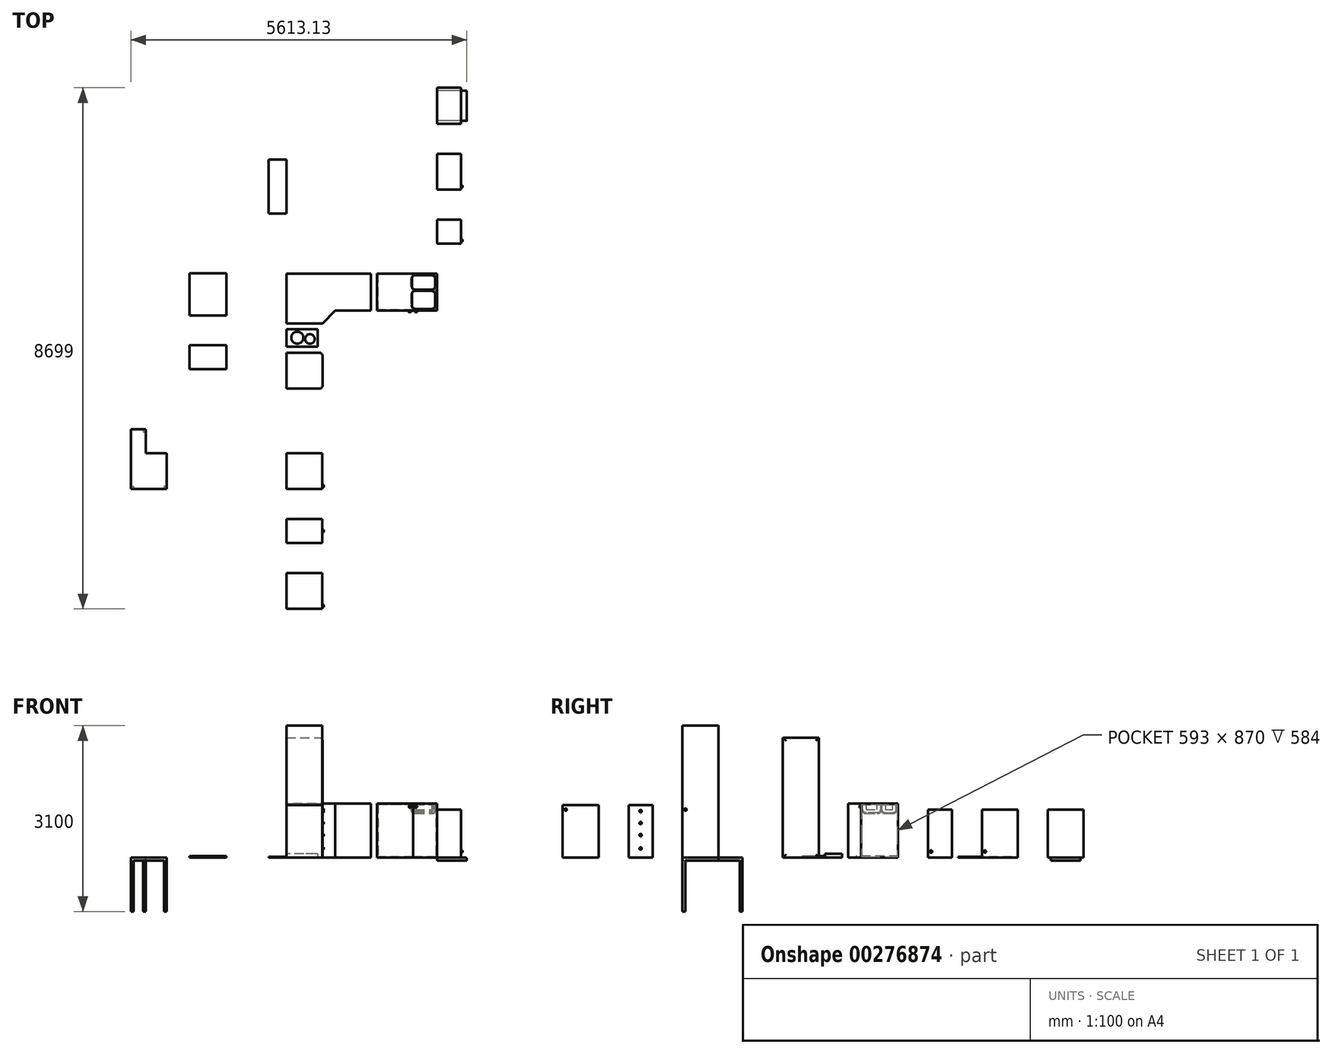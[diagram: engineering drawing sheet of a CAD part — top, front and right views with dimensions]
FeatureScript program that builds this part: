
annotation { "Feature Type Name" : "Feature", "Feature Type Description" : "" }
export const myFeature = defineFeature(function(context is Context, id is Id, definition is map)
    precondition{}
    {
        {
            var Q0;
            Q0=qCreatedBy(makeId("Top.planeOp"),FACE);
            var sketch = newSketch(context, id + "F0", { "sketchPlane" : qUnion([Q0])});
            skLineSegment(sketch, "E0.bottom", {"start": v(0, 0) * mm, "end": v(2000, 0) * mm});
            skLineSegment(sketch, "E0.left", {"start": v(0, 0) * mm, "end": v(0, -2000) * mm});
            skLineSegment(sketch, "E1", {"start": v(2000, 0) * mm, "end": v(2000, 120) * mm});
            skLineSegment(sketch, "E2", {"start": v(2000, 120) * mm, "end": v(-120, 120) * mm});
            skLineSegment(sketch, "E3", {"start": v(-120, 120) * mm, "end": v(-120, -2000) * mm});
            skLineSegment(sketch, "E4", {"start": v(-120, -2000) * mm, "end": v(0, -2000) * mm});
            skLineSegment(sketch, "E5", {"start": v(1300, 120) * mm, "end": v(1300, 0) * mm});
            skPoint(sketch, "E5.endSnap0", {"position": v(1000, 0) * mm});
            skLineSegment(sketch, "E6", {"start": v(1900, 120) * mm, "end": v(1900, 0) * mm});
            skSolve(sketch);
        }
        {
            var Q0;
            Q0=qCreatedBy(makeId("Top.planeOp"),FACE);
            var sketch = newSketch(context, id + "F1", { "sketchPlane" : qUnion([Q0])});
            skLineSegment(sketch, "E7.bottom", {"start": v(1, -1323.13) * mm, "end": v(601, -1323.13) * mm});
            skLineSegment(sketch, "E7.top", {"start": v(1, -1923.13) * mm, "end": v(601, -1923.13) * mm});
            skLineSegment(sketch, "E7.left", {"start": v(1, -1323.13) * mm, "end": v(1, -1923.13) * mm});
            skLineSegment(sketch, "E7.right", {"start": v(601, -1323.13) * mm, "end": v(601, -1923.13) * mm});
            skLineSegment(sketch, "E8.bottom", {"start": v(521, -1223.13) * mm, "end": v(1, -1223.13) * mm});
            skLineSegment(sketch, "E8.top", {"start": v(521, -933.13) * mm, "end": v(1, -933.13) * mm});
            skLineSegment(sketch, "E8.left", {"start": v(521, -1223.13) * mm, "end": v(521, -933.13) * mm});
            skLineSegment(sketch, "E8.right", {"start": v(1, -1223.13) * mm, "end": v(1, -933.13) * mm});
            skLineSegment(sketch, "E9", {"start": v(601, -833.13) * mm, "end": v(813.13, -621) * mm});
            skLineSegment(sketch, "E10", {"start": v(813.13, -621) * mm, "end": v(1413.13, -621) * mm});
            skLineSegment(sketch, "E11", {"start": v(1413.13, -621) * mm, "end": v(1413.13, -1) * mm});
            skLineSegment(sketch, "E12", {"start": v(1413.13, -1) * mm, "end": v(1, -1) * mm});
            skLineSegment(sketch, "E13", {"start": v(1, -1) * mm, "end": v(1, -833.13) * mm});
            skLineSegment(sketch, "E14", {"start": v(1, -833.13) * mm, "end": v(601, -833.13) * mm});
            skLineSegment(sketch, "E15.bottom", {"start": v(2513.13, -621) * mm, "end": v(1513.13, -621) * mm});
            skLineSegment(sketch, "E15.top", {"start": v(2513.13, -1) * mm, "end": v(1513.13, -1) * mm});
            skLineSegment(sketch, "E15.left", {"start": v(2513.13, -621) * mm, "end": v(2513.13, -1) * mm});
            skLineSegment(sketch, "E15.right", {"start": v(1513.13, -621) * mm, "end": v(1513.13, -1) * mm});
            skCircle(sketch, "E16", {"center": v(391, -1093.13) * mm, "radius": 80 * mm});
            skCircle(sketch, "E17", {"center": v(181, -1073.13) * mm, "radius": 100 * mm});
            skLineSegment(sketch, "E18.bottom", {"start": v(0, -4100) * mm, "end": v(0, -4500) * mm});
            skLineSegment(sketch, "E18.top", {"start": v(600, -4100) * mm, "end": v(600, -4500) * mm});
            skLineSegment(sketch, "E18.left", {"start": v(0, -4100) * mm, "end": v(600, -4100) * mm});
            skLineSegment(sketch, "E18.right", {"start": v(0, -4500) * mm, "end": v(600, -4500) * mm});
            skLineSegment(sketch, "E19.left", {"start": v(2513.13, 3099) * mm, "end": v(2513.13, 2499) * mm});
            skLineSegment(sketch, "E19.right", {"start": v(3013.13, 3049) * mm, "end": v(3013.13, 2549) * mm});
            skLineSegment(sketch, "E20", {"start": v(2913.13, 3099) * mm, "end": v(2913.13, 2499) * mm});
            skLineSegment(sketch, "E21.bottom", {"start": v(2513.13, 499) * mm, "end": v(2913.13, 499) * mm});
            skLineSegment(sketch, "E21.top", {"start": v(2513.13, 899) * mm, "end": v(2913.13, 899) * mm});
            skLineSegment(sketch, "E21.left", {"start": v(2513.13, 499) * mm, "end": v(2513.13, 899) * mm});
            skLineSegment(sketch, "E21.right", {"start": v(2913.13, 499) * mm, "end": v(2913.13, 899) * mm});
            skLineSegment(sketch, "E22.bottom", {"start": v(-1620, 0) * mm, "end": v(-1000, 0) * mm});
            skLineSegment(sketch, "E22.top", {"start": v(-1620, -700) * mm, "end": v(-1000, -700) * mm});
            skLineSegment(sketch, "E22.left", {"start": v(-1620, 0) * mm, "end": v(-1620, -700) * mm});
            skLineSegment(sketch, "E22.right", {"start": v(-1000, 0) * mm, "end": v(-1000, -700) * mm});
            skLineSegment(sketch, "E23", {"start": v(2513.13, 2499) * mm, "end": v(2913.13, 2499) * mm});
            skLineSegment(sketch, "E24", {"start": v(2513.13, 3099) * mm, "end": v(2913.13, 3099) * mm});
            skLineSegment(sketch, "E25", {"start": v(3013.13, 3049) * mm, "end": v(2913.13, 3049) * mm});
            skLineSegment(sketch, "E26", {"start": v(3013.13, 2549) * mm, "end": v(2913.13, 2549) * mm});
            skLineSegment(sketch, "E27", {"start": v(2913.13, 3049) * mm, "end": v(2513.13, 3049) * mm});
            skLineSegment(sketch, "E28", {"start": v(2913.13, 2549) * mm, "end": v(2513.13, 2549) * mm});
            skLineSegment(sketch, "E29.bottom", {"start": v(2513.13, 1399) * mm, "end": v(2913.13, 1399) * mm});
            skLineSegment(sketch, "E29.top", {"start": v(2513.13, 1999) * mm, "end": v(2913.13, 1999) * mm});
            skLineSegment(sketch, "E29.left", {"start": v(2513.13, 1399) * mm, "end": v(2513.13, 1999) * mm});
            skLineSegment(sketch, "E29.right", {"start": v(2913.13, 1399) * mm, "end": v(2913.13, 1999) * mm});
            skLineSegment(sketch, "E30.bottom", {"start": v(0, -3000) * mm, "end": v(600, -3000) * mm});
            skLineSegment(sketch, "E30.top", {"start": v(0, -3600) * mm, "end": v(600, -3600) * mm});
            skLineSegment(sketch, "E30.left", {"start": v(0, -3000) * mm, "end": v(0, -3600) * mm});
            skLineSegment(sketch, "E30.right", {"start": v(600, -3000) * mm, "end": v(600, -3600) * mm});
            skLineSegment(sketch, "E31.bottom", {"start": v(0, -5000) * mm, "end": v(600, -5000) * mm});
            skLineSegment(sketch, "E31.top", {"start": v(0, -5600) * mm, "end": v(600, -5600) * mm});
            skLineSegment(sketch, "E31.left", {"start": v(0, -5000) * mm, "end": v(0, -5600) * mm});
            skLineSegment(sketch, "E31.right", {"start": v(600, -5000) * mm, "end": v(600, -5600) * mm});
            skLineSegment(sketch, "E32.bottom", {"start": v(-1000, -1200) * mm, "end": v(-1620, -1200) * mm});
            skLineSegment(sketch, "E32.top", {"start": v(-1000, -1600) * mm, "end": v(-1620, -1600) * mm});
            skLineSegment(sketch, "E32.left", {"start": v(-1000, -1200) * mm, "end": v(-1000, -1600) * mm});
            skLineSegment(sketch, "E32.right", {"start": v(-1620, -1200) * mm, "end": v(-1620, -1600) * mm});
            skLineSegment(sketch, "E33.bottom", {"start": v(-300, 1900) * mm, "end": v(0, 1900) * mm});
            skLineSegment(sketch, "E33.top", {"start": v(-300, 1000) * mm, "end": v(0, 1000) * mm});
            skLineSegment(sketch, "E33.left", {"start": v(0, 1900) * mm, "end": v(0, 1000) * mm});
            skLineSegment(sketch, "E33.right", {"start": v(-300, 1900) * mm, "end": v(-300, 1000) * mm});
            skLineSegment(sketch, "E34", {"start": v(-2350, -2600) * mm, "end": v(-2350, -3000) * mm});
            skLineSegment(sketch, "E35", {"start": v(-2350, -3000) * mm, "end": v(-2000, -3000) * mm});
            skLineSegment(sketch, "E36", {"start": v(-2000, -3000) * mm, "end": v(-2000, -3600) * mm});
            skLineSegment(sketch, "E37", {"start": v(-2000, -3600) * mm, "end": v(-2600, -3600) * mm});
            skLineSegment(sketch, "E38", {"start": v(-2600, -3600) * mm, "end": v(-2600, -2600) * mm});
            skLineSegment(sketch, "E39", {"start": v(-2600, -2600) * mm, "end": v(-2350, -2600) * mm});
            skLineSegment(sketch, "E40", {"start": v(-2395, -2600) * mm, "end": v(-2395, -2645) * mm});
            skLineSegment(sketch, "E41", {"start": v(-2395, -2645) * mm, "end": v(-2350, -2645) * mm});
            skLineSegment(sketch, "E42", {"start": v(-2600, -3555) * mm, "end": v(-2555, -3555) * mm});
            skLineSegment(sketch, "E43", {"start": v(-2555, -3555) * mm, "end": v(-2555, -3600) * mm});
            skLineSegment(sketch, "E44", {"start": v(-2000, -3555) * mm, "end": v(-2045, -3555) * mm});
            skLineSegment(sketch, "E45", {"start": v(-2045, -3555) * mm, "end": v(-2045, -3600) * mm});
            skSolve(sketch);
        }
        {
            var Q0;
            Q0=makeQuery(id+"F1.imprint","IMPRINT",FACE,{"disambiguationData":[TD([[makeQuery(id+"F1.imprint","IMPRINT",EDGE,{"derivedFrom":sQuery(id+"F1.wireOp",EDGE,"E7.bottom")}),-1.0]])]});
            extrude(context, id + "F2", {"entities" : qUnion([Q0]), "depth" : 2000 * mm});
        }
        {
            var Q0;
            Q0=makeQuery(id+"F1.imprint","IMPRINT",FACE,{"disambiguationData":[TD([[makeQuery(id+"F1.imprint","IMPRINT",EDGE,{"derivedFrom":sQuery(id+"F1.wireOp",EDGE,"E8.bottom")}),-1.0]])]});
            extrude(context, id + "F3", {"entities" : qUnion([Q0]), "depth" : 60 * mm});
        }
        {
            var Q0;
            Q0=makeQuery(id+"F1.imprint","IMPRINT",FACE,{"disambiguationData":[TD([[makeQuery(id+"F1.imprint","IMPRINT",EDGE,{"derivedFrom":sQuery(id+"F1.wireOp",EDGE,"E9")}),1.0]])]});
            extrude(context, id + "F4", {"entities" : qUnion([Q0]), "depth" : 900 * mm});
        }
        {
            var Q0;
            Q0=makeQuery(id+"F1.imprint","IMPRINT",FACE,{"disambiguationData":[TD([[makeQuery(id+"F1.imprint","IMPRINT",EDGE,{"derivedFrom":sQuery(id+"F1.wireOp",EDGE,"E15.bottom")}),-1.0]])]});
            extrude(context, id + "F5", {"entities" : qUnion([Q0]), "depth" : 900 * mm});
        }
        {
            var Q0;
            Q0=makeQuery(id+"F5.opExtrude","CAP_FACE",FACE,{"disambiguationData":[OSD([sQuery(id+"F1.wireOp",EDGE,"E15.bottom"),sQuery(id+"F1.wireOp",EDGE,"E15.top"),sQuery(id+"F1.wireOp",EDGE,"E15.left"),sQuery(id+"F1.wireOp",EDGE,"E15.right")])],"isStart":false});
            var sketch = newSketch(context, id + "F6", { "sketchPlane" : qUnion([Q0])});
            skLineSegment(sketch, "E46.bottom", {"start": v(2153.13, -291) * mm, "end": v(2423.13, -291) * mm});
            skLineSegment(sketch, "E46.top", {"start": v(2153.13, -591) * mm, "end": v(2423.13, -591) * mm});
            skLineSegment(sketch, "E46.left", {"start": v(2093.13, -351) * mm, "end": v(2093.13, -531) * mm});
            skLineSegment(sketch, "E46.right", {"start": v(2483.13, -351) * mm, "end": v(2483.13, -531) * mm});
            skPoint(sketch, "E47.visualSharp", {"position": v(2093.13, -291) * mm});
            skArc(sketch, "E47.filletArc", {"start": v(2153.13, -291) * mm, "mid": v(2110.7, -308.57) * mm, "end": v(2093.13, -351) * mm});
            skPoint(sketch, "E48.visualSharp", {"position": v(2483.13, -291) * mm});
            skArc(sketch, "E48.filletArc", {"start": v(2483.13, -351) * mm, "mid": v(2465.56, -308.57) * mm, "end": v(2423.13, -291) * mm});
            skPoint(sketch, "E49.visualSharp", {"position": v(2483.13, -591) * mm});
            skArc(sketch, "E49.filletArc", {"start": v(2423.13, -591) * mm, "mid": v(2465.56, -573.43) * mm, "end": v(2483.13, -531) * mm});
            skPoint(sketch, "E50.visualSharp", {"position": v(2093.13, -591) * mm});
            skArc(sketch, "E50.filletArc", {"start": v(2093.13, -531) * mm, "mid": v(2110.7, -573.43) * mm, "end": v(2153.13, -591) * mm});
            skLineSegment(sketch, "E51.bottom", {"start": v(2153.13, -271) * mm, "end": v(2423.13, -271) * mm});
            skLineSegment(sketch, "E51.top", {"start": v(2153.13, -31) * mm, "end": v(2423.13, -31) * mm});
            skLineSegment(sketch, "E51.left", {"start": v(2093.13, -211) * mm, "end": v(2093.13, -91) * mm});
            skLineSegment(sketch, "E51.right", {"start": v(2483.13, -211) * mm, "end": v(2483.13, -91) * mm});
            skPoint(sketch, "E52.visualSharp", {"position": v(2483.13, -31) * mm});
            skArc(sketch, "E52.filletArc", {"start": v(2483.13, -91) * mm, "mid": v(2465.56, -48.57) * mm, "end": v(2423.13, -31) * mm});
            skPoint(sketch, "E53.visualSharp", {"position": v(2483.13, -271) * mm});
            skArc(sketch, "E53.filletArc", {"start": v(2423.13, -271) * mm, "mid": v(2465.56, -253.43) * mm, "end": v(2483.13, -211) * mm});
            skPoint(sketch, "E54.visualSharp", {"position": v(2093.13, -271) * mm});
            skArc(sketch, "E54.filletArc", {"start": v(2093.13, -211) * mm, "mid": v(2110.7, -253.43) * mm, "end": v(2153.13, -271) * mm});
            skPoint(sketch, "E55.visualSharp", {"position": v(2093.13, -31) * mm});
            skArc(sketch, "E55.filletArc", {"start": v(2153.13, -31) * mm, "mid": v(2110.7, -48.57) * mm, "end": v(2093.13, -91) * mm});
            skSolve(sketch);
        }
        {
            var Q0;
            Q0 = qSketchRegion(id + "F6", true);
            extrude(context, id + "F7", {"entities" : qUnion([Q0]), "operationType" : NewBodyOperationType.REMOVE, "oppositeDirection" : true, "depth" : 150 * mm});
        }
        {
            var Q0;
            Q0=makeQuery(id+"F7.boolean.opBoolean","COPY",EDGE,{"derivedFrom":makeQuery(id+"F7.opExtrude","CAP_EDGE",EDGE,{"disambiguationData":[OSD([sQuery(id+"F6.wireOp",EDGE,"E46.bottom")])],"isStart":false})});
            var Q1;
            Q1=makeQuery(id+"F7.boolean.opBoolean","COPY",EDGE,{"derivedFrom":makeQuery(id+"F7.opExtrude","CAP_EDGE",EDGE,{"disambiguationData":[OSD([sQuery(id+"F6.wireOp",EDGE,"E51.top")])],"isStart":false})});
            fillet(context, id + "F8", {"entities" : qUnion([Q0, Q1]), "radius" : 50 * mm, "tangentPropagation" : true, "allowEdgeOverflow" : false});
        }
        {
            var Q0;
            Q0=makeQuery(id+"F5.opExtrude","SWEPT_FACE",FACE,{"disambiguationData":[OSD([sQuery(id+"F1.wireOp",EDGE,"E15.bottom")])]});
            shell(context, id + "F9", {"entities" : qUnion([Q0]), "thickness" : 15 * mm});
        }
        {
            var Q0;
            Q0=makeQuery(id+"F1.imprint","IMPRINT",FACE,{"disambiguationData":[TD([[makeQuery(id+"F1.imprint","IMPRINT",EDGE,{"derivedFrom":sQuery(id+"F1.wireOp",EDGE,"E17")}),1.0]])]});
            var Q1;
            Q1=makeQuery(id+"F1.imprint","IMPRINT",FACE,{"disambiguationData":[TD([[makeQuery(id+"F1.imprint","IMPRINT",EDGE,{"derivedFrom":sQuery(id+"F1.wireOp",EDGE,"E16")}),1.0]])]});
            extrude(context, id + "F10", {"entities" : qUnion([Q0, Q1]), "operationType" : NewBodyOperationType.ADD, "depth" : 61 * mm});
        }
        {
            var Q0;
            Q0=makeQuery(id+"F1.imprint","IMPRINT",FACE,{"disambiguationData":[TD([[makeQuery(id+"F1.imprint","IMPRINT",EDGE,{"derivedFrom":sQuery(id+"F1.wireOp",EDGE,"E18.bottom")}),1.0]])]});
            var Q1;
            Q1=makeQuery(id+"F1.imprint","IMPRINT",FACE,{"disambiguationData":[TD([[makeQuery(id+"F1.imprint","IMPRINT",EDGE,{"derivedFrom":sQuery(id+"F1.wireOp",EDGE,"E31.bottom")}),-1.0]])]});
            var Q2;
            Q2=makeQuery(id+"F3.opExtrude","CAP_FACE",FACE,{"disambiguationData":[OSD([sQuery(id+"F1.wireOp",EDGE,"E8.bottom"),sQuery(id+"F1.wireOp",EDGE,"E8.top"),sQuery(id+"F1.wireOp",EDGE,"E8.left"),sQuery(id+"F1.wireOp",EDGE,"E8.right"),sQuery(id+"F1.wireOp",EDGE,"E16"),sQuery(id+"F1.wireOp",EDGE,"E17")])],"isStart":false});
            extrude(context, id + "F11", {"entities" : qUnion([Q0, Q1]), "endBoundEntityFace" : qUnion([Q2]), "depth" : 875 * mm});
        }
        {
            var Q0;
            {var subQ0=sQuery(id+"F1.wireOp",EDGE,"E19.left");Q0=makeQuery(id+"F1.imprint","IMPRINT",FACE,{"disambiguationData":[TD([[makeQuery(id+"F1.imprint","IMPRINT",EDGE,{"derivedFrom":subQ0}),1.0]])]});}
            extrude(context, id + "F12", {"entities" : qUnion([Q0]), "depth" : 800 * mm});
        }
        {
            var Q0;
            {var subQ0=sQuery(id+"F1.wireOp",EDGE,"E19.right");Q0=makeQuery(id+"F1.imprint","IMPRINT",FACE,{"disambiguationData":[TD([[makeQuery(id+"F1.imprint","IMPRINT",EDGE,{"derivedFrom":subQ0}),-1.0]])]});}
            var Q1;
            {var subQ0=sQuery(id+"F1.wireOp",EDGE,"E27");Q1=makeQuery(id+"F1.imprint","IMPRINT",FACE,{"disambiguationData":[TD([[makeQuery(id+"F1.imprint","IMPRINT",EDGE,{"derivedFrom":subQ0}),1.0]])]});}
            extrude(context, id + "F13", {"entities" : qUnion([Q0, Q1]), "operationType" : NewBodyOperationType.ADD, "oppositeDirection" : true, "depth" : 50 * mm});
        }
        {
            var Q0;
            Q0=makeQuery(id+"F13.opExtrude","CAP_EDGE",EDGE,{"disambiguationData":[OSD([sQuery(id+"F1.wireOp",EDGE,"E19.right")])],"isStart":true});
            fillet(context, id + "F14", {"entities" : qUnion([Q0]), "radius" : 30 * mm, "tangentPropagation" : true, "allowEdgeOverflow" : false});
        }
        {
            var Q0;
            Q0=makeQuery(id+"F1.imprint","IMPRINT",FACE,{"disambiguationData":[TD([[makeQuery(id+"F1.imprint","IMPRINT",EDGE,{"derivedFrom":sQuery(id+"F1.wireOp",EDGE,"E21.bottom")}),1.0]])]});
            var Q1;
            Q1=makeQuery(id+"F1.imprint","IMPRINT",FACE,{"disambiguationData":[TD([[makeQuery(id+"F1.imprint","IMPRINT",EDGE,{"derivedFrom":sQuery(id+"F1.wireOp",EDGE,"E29.bottom")}),1.0]])]});
            extrude(context, id + "F15", {"entities" : qUnion([Q0, Q1]), "depth" : 800 * mm});
        }
        {
            var Q0;
            Q0=makeQuery(id+"F1.imprint","IMPRINT",FACE,{"disambiguationData":[TD([[makeQuery(id+"F1.imprint","IMPRINT",EDGE,{"derivedFrom":sQuery(id+"F1.wireOp",EDGE,"E22.bottom")}),-1.0]])]});
            var Q1;
            Q1=makeQuery(id+"F1.imprint","IMPRINT",FACE,{"disambiguationData":[TD([[makeQuery(id+"F1.imprint","IMPRINT",EDGE,{"derivedFrom":sQuery(id+"F1.wireOp",EDGE,"E32.bottom")}),1.0]])]});
            extrude(context, id + "F16", {"entities" : qUnion([Q0, Q1]), "depth" : 25 * mm});
        }
        {
            var Q0;
            Q0=makeQuery(id+"F15.opExtrude","SWEPT_FACE",FACE,{"disambiguationData":[OSD([sQuery(id+"F1.wireOp",EDGE,"E21.right")])]});
            var sketch = newSketch(context, id + "F17", { "sketchPlane" : qUnion([Q0])});
            skCircle(sketch, "E56", {"center": v(549, 100) * mm, "radius": 20 * mm});
            skCircle(sketch, "E57", {"center": v(1449, 100) * mm, "radius": 20 * mm});
            skSolve(sketch);
        }
        {
            var Q0;
            Q0 = qSketchRegion(id + "F17", true);
            extrude(context, id + "F18", {"entities" : qUnion([Q0]), "operationType" : NewBodyOperationType.ADD, "depth" : 25 * mm});
        }
        {
            var Q0;
            Q0=makeQuery(id+"F1.imprint","IMPRINT",FACE,{"disambiguationData":[TD([[makeQuery(id+"F1.imprint","IMPRINT",EDGE,{"derivedFrom":sQuery(id+"F1.wireOp",EDGE,"E30.bottom")}),-1.0]])]});
            extrude(context, id + "F19", {"entities" : qUnion([Q0]), "depth" : 2200 * mm});
        }
        {
            var Q0;
            Q0=makeQuery(id+"F11.opExtrude","SWEPT_FACE",FACE,{"disambiguationData":[OSD([sQuery(id+"F1.wireOp",EDGE,"E18.top")])]});
            var sketch = newSketch(context, id + "F20", { "sketchPlane" : qUnion([Q0])});
            skCircle(sketch, "E58", {"center": v(-4300, 150) * mm, "radius": 20 * mm});
            skCircle(sketch, "E59", {"center": v(-3550, 800) * mm, "radius": 20 * mm});
            skCircle(sketch, "E60", {"center": v(-4300, 375) * mm, "radius": 20 * mm});
            skCircle(sketch, "E61", {"center": v(-4300, 575) * mm, "radius": 20 * mm});
            skCircle(sketch, "E62", {"center": v(-4300, 775) * mm, "radius": 20 * mm});
            skCircle(sketch, "E63", {"center": v(-5550, 800) * mm, "radius": 20 * mm});
            skSolve(sketch);
        }
        {
            var Q0;
            Q0=makeQuery(id+"F20.imprint","IMPRINT",FACE,{"disambiguationData":[TD([[makeQuery(id+"F20.imprint","IMPRINT",EDGE,{"derivedFrom":sQuery(id+"F20.wireOp",EDGE,"E58")}),1.0]])]});
            var Q1;
            Q1=makeQuery(id+"F20.imprint","IMPRINT",FACE,{"disambiguationData":[TD([[makeQuery(id+"F20.imprint","IMPRINT",EDGE,{"derivedFrom":sQuery(id+"F20.wireOp",EDGE,"E59")}),1.0]])]});
            var Q2;
            Q2=makeQuery(id+"F20.imprint","IMPRINT",FACE,{"disambiguationData":[TD([[makeQuery(id+"F20.imprint","IMPRINT",EDGE,{"derivedFrom":sQuery(id+"F20.wireOp",EDGE,"E60")}),1.0]])]});
            var Q3;
            Q3=makeQuery(id+"F20.imprint","IMPRINT",FACE,{"disambiguationData":[TD([[makeQuery(id+"F20.imprint","IMPRINT",EDGE,{"derivedFrom":sQuery(id+"F20.wireOp",EDGE,"E61")}),1.0]])]});
            var Q4;
            Q4=makeQuery(id+"F20.imprint","IMPRINT",FACE,{"disambiguationData":[TD([[makeQuery(id+"F20.imprint","IMPRINT",EDGE,{"derivedFrom":sQuery(id+"F20.wireOp",EDGE,"E62")}),1.0]])]});
            var Q5;
            Q5=makeQuery(id+"F20.imprint","IMPRINT",FACE,{"disambiguationData":[TD([[makeQuery(id+"F20.imprint","IMPRINT",EDGE,{"derivedFrom":sQuery(id+"F20.wireOp",EDGE,"E63")}),1.0]])]});
            extrude(context, id + "F21", {"entities" : qUnion([Q0, Q1, Q2, Q3, Q4, Q5]), "operationType" : NewBodyOperationType.ADD, "depth" : 25 * mm});
        }
        {
            var Q0;
            Q0=makeQuery(id+"F2.opExtrude","SWEPT_EDGE",EDGE,{"disambiguationData":[OSD([sQuery(id+"F1.wireOp",EDGE,"E7.top"),sQuery(id+"F1.wireOp",EDGE,"E7.right")])]});
            var Q1;
            Q1=makeQuery(id+"F2.opExtrude","SWEPT_EDGE",EDGE,{"disambiguationData":[OSD([sQuery(id+"F1.wireOp",EDGE,"E7.bottom"),sQuery(id+"F1.wireOp",EDGE,"E7.right")])]});
            var Q2;
            Q2=makeQuery(id+"F2.opExtrude","CAP_EDGE",EDGE,{"disambiguationData":[OSD([sQuery(id+"F1.wireOp",EDGE,"E7.right")])],"isStart":false});
            var Q3;
            Q3=makeQuery(id+"F2.opExtrude","CAP_EDGE",EDGE,{"disambiguationData":[OSD([sQuery(id+"F1.wireOp",EDGE,"E7.right")])],"isStart":true});
            fillet(context, id + "F22", {"entities" : qUnion([Q0, Q1, Q2, Q3]), "radius" : 50 * mm, "tangentPropagation" : true, "allowEdgeOverflow" : false});
        }
        {
            var Q0;
            Q0=makeQuery(id+"F5.opExtrude","SWEPT_FACE",FACE,{"disambiguationData":[OSD([sQuery(id+"F1.wireOp",EDGE,"E15.bottom")])]});
            var sketch = newSketch(context, id + "F23", { "sketchPlane" : qUnion([Q0])});
            skLineSegment(sketch, "E64.bottom", {"start": v(1513.13, 900) * mm, "end": v(2112.13, 900) * mm});
            skLineSegment(sketch, "E64.top", {"start": v(1513.13, 0) * mm, "end": v(2112.13, 0) * mm});
            skLineSegment(sketch, "E64.left", {"start": v(1513.13, 900) * mm, "end": v(1513.13, 0) * mm});
            skLineSegment(sketch, "E64.right", {"start": v(2513.13, 900) * mm, "end": v(2513.13, 0) * mm});
            skLineSegment(sketch, "E65", {"start": v(2112.13, 900) * mm, "end": v(2112.13, 0) * mm});
            skLineSegment(sketch, "E66", {"start": v(2113.13, 900) * mm, "end": v(2113.13, 0) * mm});
            skLineSegment(sketch, "E67.trimOffspring", {"start": v(2113.13, 900) * mm, "end": v(2513.13, 900) * mm});
            skLineSegment(sketch, "E68.trimOffspring", {"start": v(2113.13, 0) * mm, "end": v(2513.13, 0) * mm});
            skCircle(sketch, "E69", {"center": v(2063.13, 850) * mm, "radius": 20 * mm});
            skCircle(sketch, "E70", {"center": v(2163.13, 850) * mm, "radius": 20 * mm});
            skSolve(sketch);
        }
        {
            var Q0;
            Q0=makeQuery(id+"F23.imprint","IMPRINT",FACE,{"disambiguationData":[TD([[makeQuery(id+"F23.imprint","IMPRINT",EDGE,{"derivedFrom":sQuery(id+"F23.wireOp",EDGE,"E69")}),-1.0]])]});
            var Q1;
            Q1=makeQuery(id+"F23.imprint","IMPRINT",FACE,{"disambiguationData":[TD([[makeQuery(id+"F23.imprint","IMPRINT",EDGE,{"derivedFrom":sQuery(id+"F23.wireOp",EDGE,"E70")}),-1.0]])]});
            extrude(context, id + "F24", {"entities" : qUnion([Q0, Q1]), "operationType" : NewBodyOperationType.ADD, "oppositeDirection" : true, "depth" : 12 * mm});
        }
        {
            var Q0;
            Q0=makeQuery(id+"F23.imprint","IMPRINT",FACE,{"disambiguationData":[TD([[makeQuery(id+"F23.imprint","IMPRINT",EDGE,{"derivedFrom":sQuery(id+"F23.wireOp",EDGE,"E69")}),1.0]])]});
            var Q1;
            Q1=makeQuery(id+"F23.imprint","IMPRINT",FACE,{"disambiguationData":[TD([[makeQuery(id+"F23.imprint","IMPRINT",EDGE,{"derivedFrom":sQuery(id+"F23.wireOp",EDGE,"E70")}),1.0]])]});
            extrude(context, id + "F25", {"entities" : qUnion([Q0, Q1]), "operationType" : NewBodyOperationType.ADD, "depth" : 25 * mm, "hasSecondDirection" : true, "secondDirectionOppositeDirection" : true, "secondDirectionDepth" : 12 * mm});
        }
        {
            var Q0;
            Q0=makeQuery(id+"F1.imprint","IMPRINT",FACE,{"disambiguationData":[TD([[makeQuery(id+"F1.imprint","IMPRINT",EDGE,{"derivedFrom":sQuery(id+"F1.wireOp",EDGE,"E33.bottom")}),-1.0]])]});
            extrude(context, id + "F26", {"entities" : qUnion([Q0]), "depth" : 9 * mm});
        }
        {
            var Q0;
            {var subQ6=sQuery(id+"F1.wireOp",EDGE,"E35");Q0=makeQuery(id+"F1.imprint","IMPRINT",FACE,{"disambiguationData":[TD([[makeQuery(id+"F1.imprint","IMPRINT",EDGE,{"derivedFrom":subQ6}),-1.0]])]});}
            var Q1;
            {var subQ4=sQuery(id+"F1.wireOp",EDGE,"E40");Q1=makeQuery(id+"F1.imprint","IMPRINT",FACE,{"disambiguationData":[TD([[makeQuery(id+"F1.imprint","IMPRINT",EDGE,{"derivedFrom":subQ4}),1.0]])]});}
            var Q2;
            {var subQ4=sQuery(id+"F1.wireOp",EDGE,"E42");Q2=makeQuery(id+"F1.imprint","IMPRINT",FACE,{"disambiguationData":[TD([[makeQuery(id+"F1.imprint","IMPRINT",EDGE,{"derivedFrom":subQ4}),-1.0]])]});}
            var Q3;
            {var subQ3=sQuery(id+"F1.wireOp",EDGE,"E44");Q3=makeQuery(id+"F1.imprint","IMPRINT",FACE,{"disambiguationData":[TD([[makeQuery(id+"F1.imprint","IMPRINT",EDGE,{"derivedFrom":subQ3}),1.0]])]});}
            extrude(context, id + "F27", {"entities" : qUnion([Q0, Q1, Q2, Q3]), "oppositeDirection" : true, "depth" : 50 * mm});
        }
        {
            var Q0;
            {var subQ4=sQuery(id+"F1.wireOp",EDGE,"E42");Q0=makeQuery(id+"F1.imprint","IMPRINT",FACE,{"disambiguationData":[TD([[makeQuery(id+"F1.imprint","IMPRINT",EDGE,{"derivedFrom":subQ4}),-1.0]])]});}
            var Q1;
            {var subQ3=sQuery(id+"F1.wireOp",EDGE,"E44");Q1=makeQuery(id+"F1.imprint","IMPRINT",FACE,{"disambiguationData":[TD([[makeQuery(id+"F1.imprint","IMPRINT",EDGE,{"derivedFrom":subQ3}),1.0]])]});}
            var Q2;
            {var subQ4=sQuery(id+"F1.wireOp",EDGE,"E40");Q2=makeQuery(id+"F1.imprint","IMPRINT",FACE,{"disambiguationData":[TD([[makeQuery(id+"F1.imprint","IMPRINT",EDGE,{"derivedFrom":subQ4}),1.0]])]});}
            extrude(context, id + "F28", {"entities" : qUnion([Q0, Q1, Q2]), "operationType" : NewBodyOperationType.ADD, "oppositeDirection" : true, "depth" : 900 * mm});
        }
    });
